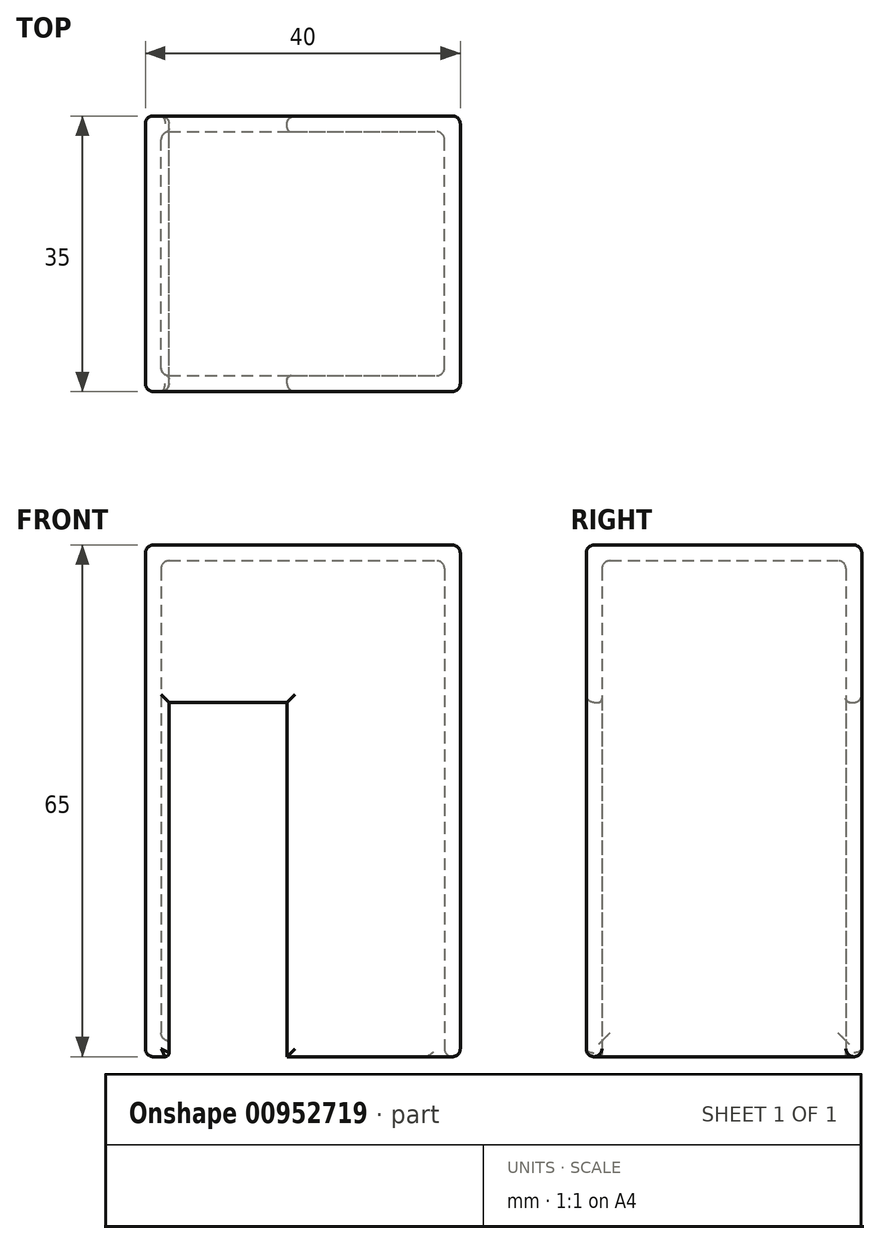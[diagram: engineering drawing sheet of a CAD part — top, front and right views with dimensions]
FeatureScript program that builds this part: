
annotation { "Feature Type Name" : "Feature", "Feature Type Description" : "" }
export const myFeature = defineFeature(function(context is Context, id is Id, definition is map)
    precondition{}
    {
        {
            var Q0;
            Q0=qCreatedBy(makeId("Front.planeOp"),FACE);
            var sketch = newSketch(context, id + "F0", { "sketchPlane" : qUnion([Q0])});
            skLineSegment(sketch, "E0.bottom", {"start": v(-20, 32.5) * mm, "end": v(20, 32.5) * mm});
            skLineSegment(sketch, "E0.top", {"start": v(-20, -32.5) * mm, "end": v(20, -32.5) * mm});
            skLineSegment(sketch, "E0.left", {"start": v(-20, 32.5) * mm, "end": v(-20, -32.5) * mm});
            skLineSegment(sketch, "E0.right", {"start": v(20, 32.5) * mm, "end": v(20, -32.5) * mm});
            skPoint(sketch, "E0.middle", {"position": v(0, 0) * mm});
            skLineSegment(sketch, "E1", {"start": v(-17, 32.5) * mm, "end": v(-17, -32.5) * mm});
            skLineSegment(sketch, "E2", {"start": v(-2, 32.5) * mm, "end": v(-2, -32.5) * mm});
            skLineSegment(sketch, "E3", {"start": v(-17, 12.5) * mm, "end": v(-2, 12.5) * mm});
            skSolve(sketch);
        }
        {
            var Q0;
            {var subQ0=sQuery(id+"F0.wireOp",EDGE,"E0.left");Q0=makeQuery(id+"F0.imprint","IMPRINT",FACE,{"disambiguationData":[TD([[makeQuery(id+"F0.imprint","IMPRINT",EDGE,{"derivedFrom":subQ0}),1.0]])]});}
            var Q1;
            {var subQ5=sQuery(id+"F0.wireOp",EDGE,"E3");Q1=makeQuery(id+"F0.imprint","IMPRINT",FACE,{"disambiguationData":[TD([[makeQuery(id+"F0.imprint","IMPRINT",EDGE,{"derivedFrom":subQ5}),1.0]])]});}
            var Q2;
            {var subQ4=sQuery(id+"F0.wireOp",EDGE,"E0.right");Q2=makeQuery(id+"F0.imprint","IMPRINT",FACE,{"disambiguationData":[TD([[makeQuery(id+"F0.imprint","IMPRINT",EDGE,{"derivedFrom":subQ4}),-1.0]])]});}
            extrude(context, id + "F1", {"entities" : qUnion([Q0, Q1, Q2]), "depth" : 35 * mm, "offsetDistance" : 25 * mm});
        }
        {
            var Q0;
            Q0=makeQuery(id+"F1.opExtrude","SWEPT_FACE",FACE,{"disambiguationData":[OSD([sQuery(id+"F0.wireOp",EDGE,"E2")])]});
            var Q1;
            {var subQ0=sQuery(id+"F0.wireOp",EDGE,"E0.top");Q1=makeQuery(id+"F1.opExtrude","SWEPT_FACE",FACE,{"disambiguationData":[OSD([subQ0]),TDD([makeQuery(id+"F0.imprint","IMPRINT",EDGE,{"disambiguationData":[TD([[makeQuery(id+"F0.imprint","INTERSECT",VERTEX,{"derivedFrom":[subQ0,sQuery(id+"F0.wireOp",EDGE,"E0.right")]}),1.0]])],"derivedFrom":subQ0})])]});}
            var Q2;
            Q2=makeQuery(id+"F1.opExtrude","SWEPT_FACE",FACE,{"disambiguationData":[OSD([sQuery(id+"F0.wireOp",EDGE,"E3")])]});
            var Q3;
            Q3=makeQuery(id+"F1.opExtrude","SWEPT_FACE",FACE,{"disambiguationData":[OSD([sQuery(id+"F0.wireOp",EDGE,"E1")])]});
            shell(context, id + "F2", {"entities" : qUnion([Q0, Q1, Q2, Q3]), "thickness" : 2 * mm});
        }
        {
            var Q0;
            Q0=makeQuery(id+"F1.opExtrude","CAP_EDGE",EDGE,{"disambiguationData":[OSD([sQuery(id+"F0.wireOp",EDGE,"E0.bottom")])],"isStart":false});
            var Q1;
            Q1=makeQuery(id+"F1.opExtrude","SWEPT_EDGE",EDGE,{"disambiguationData":[OSD([sQuery(id+"F0.wireOp",EDGE,"E0.bottom"),sQuery(id+"F0.wireOp",EDGE,"E0.right")])]});
            var Q2;
            Q2=makeQuery(id+"F1.opExtrude","CAP_EDGE",EDGE,{"disambiguationData":[OSD([sQuery(id+"F0.wireOp",EDGE,"E0.bottom")])],"isStart":true});
            var Q3;
            Q3=makeQuery(id+"F1.opExtrude","SWEPT_FACE",FACE,{"disambiguationData":[OSD([sQuery(id+"F0.wireOp",EDGE,"E0.bottom")])]});
            var Q4;
            Q4=makeQuery(id+"F1.opExtrude","SWEPT_FACE",FACE,{"disambiguationData":[OSD([sQuery(id+"F0.wireOp",EDGE,"E0.left")])]});
            var Q5;
            Q5=makeQuery(id+"F1.opExtrude","CAP_FACE",FACE,{"disambiguationData":[OSD([sQuery(id+"F0.wireOp",EDGE,"E0.bottom"),sQuery(id+"F0.wireOp",EDGE,"E0.top"),sQuery(id+"F0.wireOp",EDGE,"E0.left"),sQuery(id+"F0.wireOp",EDGE,"E0.right"),sQuery(id+"F0.wireOp",EDGE,"E1"),sQuery(id+"F0.wireOp",EDGE,"E2"),sQuery(id+"F0.wireOp",EDGE,"E3")])],"isStart":false});
            var Q6;
            Q6=makeQuery(id+"F1.opExtrude","SWEPT_FACE",FACE,{"disambiguationData":[OSD([sQuery(id+"F0.wireOp",EDGE,"E0.right")])]});
            var Q7;
            Q7=makeQuery(id+"F1.opExtrude","CAP_FACE",FACE,{"disambiguationData":[OSD([sQuery(id+"F0.wireOp",EDGE,"E0.bottom"),sQuery(id+"F0.wireOp",EDGE,"E0.top"),sQuery(id+"F0.wireOp",EDGE,"E0.left"),sQuery(id+"F0.wireOp",EDGE,"E0.right"),sQuery(id+"F0.wireOp",EDGE,"E1"),sQuery(id+"F0.wireOp",EDGE,"E2"),sQuery(id+"F0.wireOp",EDGE,"E3")])],"isStart":true});
            fillet(context, id + "F3", {"entities" : qUnion([Q0, Q1, Q2, Q3, Q4, Q5, Q6, Q7]), "radius" : 1 * mm, "tangentPropagation" : true, "allowEdgeOverflow" : false});
        }
        {
            var Q0;
            Q0=makeQuery(id+"F2.opShell","OFFSET_FACE",FACE,{"disambiguationData":[OSD([sQuery(id+"F0.wireOp",EDGE,"E0.bottom")])]});
            var Q1;
            Q1=makeQuery(id+"F2.opShell","OFFSET_FACE",FACE,{"disambiguationData":[OSD([sQuery(id+"F0.wireOp",EDGE,"E0.right")])]});
            var Q2;
            Q2=makeQuery(id+"F2.opShell","OFFSET_FACE",FACE,{"disambiguationData":[OSD([sQuery(id+"F0.wireOp",EDGE,"E0.left")])]});
            fillet(context, id + "F4", {"entities" : qUnion([Q0, Q1, Q2]), "radius" : 1 * mm, "tangentPropagation" : true, "allowEdgeOverflow" : false});
        }
        {
            var Q0;
            {var subQ0=sQuery(id+"F0.wireOp",EDGE,"E2");Q0=makeQuery(id+"F2.opShell","OFFSET_EDGE",EDGE,{"disambiguationData":[OSD([subQ0]),TDD([makeQuery(id+"F1.opExtrude","CAP_EDGE",EDGE,{"disambiguationData":[OSD([subQ0])],"isStart":true})])]});}
            var Q1;
            {var subQ0=sQuery(id+"F0.wireOp",EDGE,"E3");Q1=makeQuery(id+"F2.opShell","OFFSET_EDGE",EDGE,{"disambiguationData":[OSD([subQ0]),TDD([makeQuery(id+"F1.opExtrude","CAP_EDGE",EDGE,{"disambiguationData":[OSD([subQ0])],"isStart":true})])]});}
            var Q2;
            {var subQ0=sQuery(id+"F0.wireOp",EDGE,"E0.left");Q2=makeQuery(id+"F4.opFillet","BLEND_EDGE",EDGE,{"blendedFrom":[makeQuery(id+"F2.opShell","OFFSET_EDGE",EDGE,{"disambiguationData":[OSD([subQ0]),TDD([makeQuery(id+"F1.opExtrude","CAP_EDGE",EDGE,{"disambiguationData":[OSD([subQ0])],"isStart":true})])]}),makeQuery(id+"F1.opExtrude","SWEPT_FACE",FACE,{"disambiguationData":[OSD([sQuery(id+"F0.wireOp",EDGE,"E1")])]})],"blendedInto":[makeQuery(id+"F1.opExtrude","SWEPT_FACE",FACE,{"disambiguationData":[OSD([sQuery(id+"F0.wireOp",EDGE,"E1")])]})]});}
            var Q3;
            Q3=makeQuery(id+"F4.opFillet","BLEND_EDGE",EDGE,{"blendedFrom":[makeQuery(id+"F2.opShell","OFFSET_EDGE",EDGE,{"disambiguationData":[OSD([sQuery(id+"F0.wireOp",EDGE,"E0.top"),sQuery(id+"F0.wireOp",EDGE,"E0.left")])]}),makeQuery(id+"F1.opExtrude","SWEPT_FACE",FACE,{"disambiguationData":[OSD([sQuery(id+"F0.wireOp",EDGE,"E1")])]})],"blendedInto":[makeQuery(id+"F1.opExtrude","SWEPT_FACE",FACE,{"disambiguationData":[OSD([sQuery(id+"F0.wireOp",EDGE,"E1")])]})]});
            var Q4;
            {var subQ0=sQuery(id+"F0.wireOp",EDGE,"E0.left");Q4=makeQuery(id+"F4.opFillet","BLEND_EDGE",EDGE,{"blendedFrom":[makeQuery(id+"F2.opShell","OFFSET_EDGE",EDGE,{"disambiguationData":[OSD([subQ0]),TDD([makeQuery(id+"F1.opExtrude","CAP_EDGE",EDGE,{"disambiguationData":[OSD([subQ0])],"isStart":false})])]}),makeQuery(id+"F1.opExtrude","SWEPT_FACE",FACE,{"disambiguationData":[OSD([sQuery(id+"F0.wireOp",EDGE,"E1")])]})],"blendedInto":[makeQuery(id+"F1.opExtrude","SWEPT_FACE",FACE,{"disambiguationData":[OSD([sQuery(id+"F0.wireOp",EDGE,"E1")])]})]});}
            var Q5;
            {var subQ0=sQuery(id+"F0.wireOp",EDGE,"E2");Q5=makeQuery(id+"F2.opShell","OFFSET_EDGE",EDGE,{"disambiguationData":[OSD([subQ0]),TDD([makeQuery(id+"F1.opExtrude","CAP_EDGE",EDGE,{"disambiguationData":[OSD([subQ0])],"isStart":false})])]});}
            var Q6;
            {var subQ0=sQuery(id+"F0.wireOp",EDGE,"E3");Q6=makeQuery(id+"F2.opShell","OFFSET_EDGE",EDGE,{"disambiguationData":[OSD([subQ0]),TDD([makeQuery(id+"F1.opExtrude","CAP_EDGE",EDGE,{"disambiguationData":[OSD([subQ0])],"isStart":false})])]});}
            var Q7;
            Q7=makeQuery(id+"F1.opExtrude","SWEPT_EDGE",EDGE,{"disambiguationData":[OSD([sQuery(id+"F0.wireOp",EDGE,"E0.top"),sQuery(id+"F0.wireOp",EDGE,"E1")])]});
            fillet(context, id + "F5", {"entities" : qUnion([Q0, Q1, Q2, Q3, Q4, Q5, Q6, Q7]), "radius" : 0.5 * mm, "tangentPropagation" : true, "allowEdgeOverflow" : false});
        }
    });
